# Revit family: SPOT 900
name_source: partatom
category: Generic Models
revit_build: Autodesk Revit 2018 (Build: 20180423_1000(x64)
units: mm (PartAtom-declared; Revit-internal decimal feet)

## family parameters
Always vertical = Yes
Can host rebar = No
Cut with Voids When Loaded = No
Part Type = Normal
Room Calculation Point = No
Round Connector Dimension = Use Diameter
Shared = No
Work Plane-Based = No

## types (1)
- SPOT 900
    Art. No. = 880 400 900
    Breedte = 150 mm
    Colour = Coating wit
    Holes = 15
    Hoogte = 60 mm  [stored 0.19685 ft]
    Lengte = 1550 mm  [stored 5.0853 ft]
    Manufacturer = Masterwatt B.V.
    Model = SPOT 900
    Paneel = Metal grey
    Phase = 1
    Power (default) = 900 VA
    URL = https://masterwatt.nl
    Voltage = 230 V

note: [stored X ft] marks values corroborated as IEEE doubles in the binary element streams (Revit-internal decimal feet)

## geometry (parser evidence)
native form markers: Sweep x8
no freeform markers — native parametric forms only
